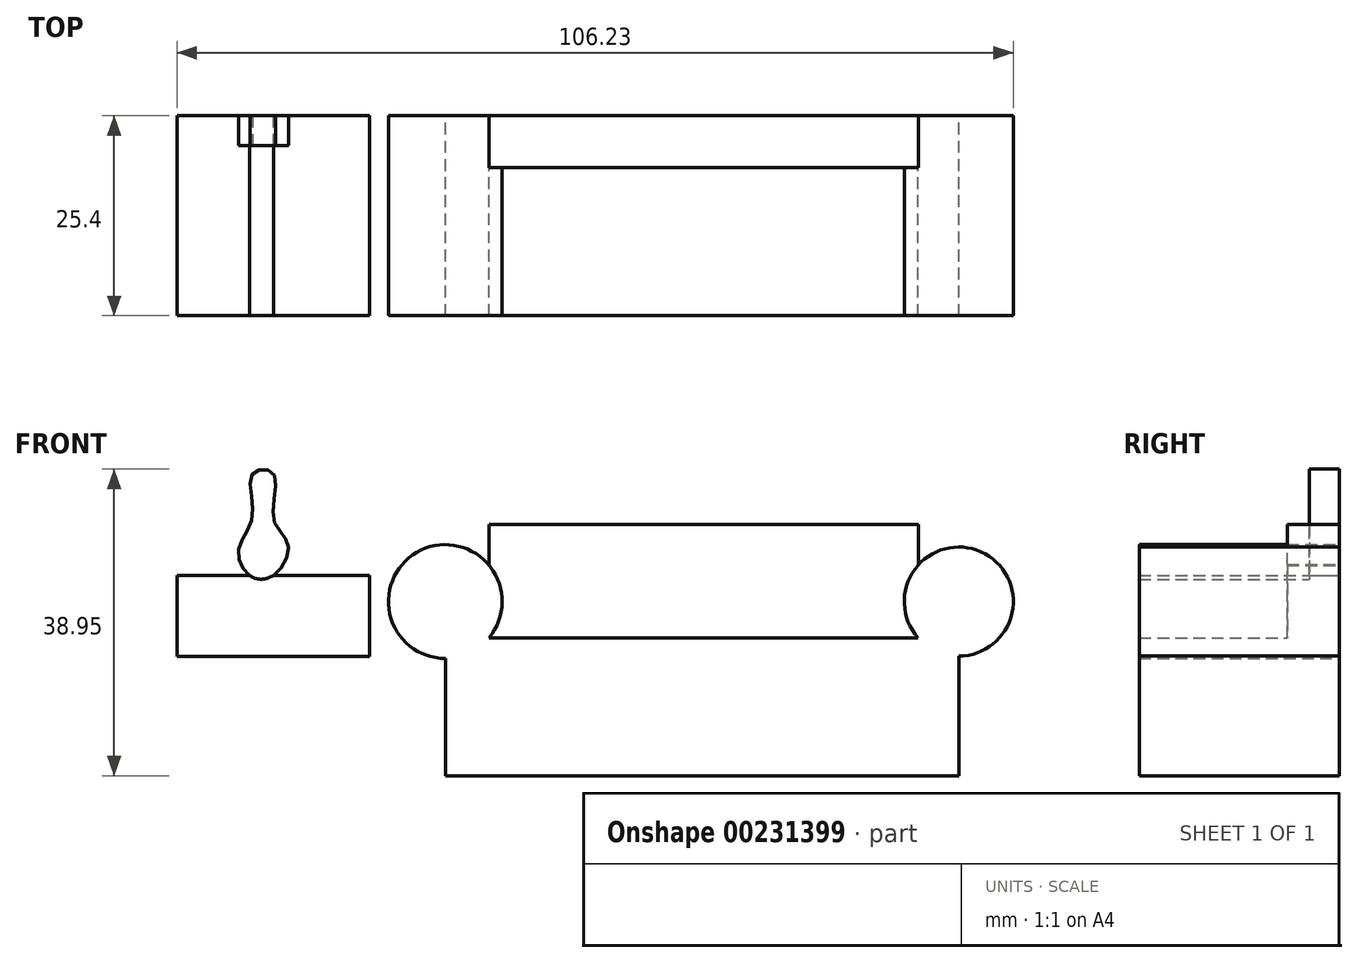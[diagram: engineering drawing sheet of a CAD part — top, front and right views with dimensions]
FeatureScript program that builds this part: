
annotation { "Feature Type Name" : "Feature", "Feature Type Description" : "" }
export const myFeature = defineFeature(function(context is Context, id is Id, definition is map)
    precondition{}
    {
        {
            var Q0;
            Q0=qCreatedBy(makeId("Front.planeOp"),FACE);
            var sketch = newSketch(context, id + "F0", { "sketchPlane" : qUnion([Q0])});
            skLineSegment(sketch, "E0.top", {"start": v(-12.93, -15.18) * mm, "end": v(52.3, -15.18) * mm});
            skLineSegment(sketch, "E0.left", {"start": v(-12.93, -0.27) * mm, "end": v(-12.93, -15.18) * mm});
            skLineSegment(sketch, "E0.right", {"start": v(52.3, 0.03) * mm, "end": v(52.3, -15.18) * mm});
            skCircle(sketch, "E1", {"center": v(-12.93, 6.95) * mm, "radius": 7.22 * mm});
            skCircle(sketch, "E2", {"center": v(52.3, 6.95) * mm, "radius": 6.92 * mm});
            skLineSegment(sketch, "E3", {"start": v(-7.36, 2.35) * mm, "end": v(47.12, 2.35) * mm});
            skLineSegment(sketch, "E4.bottom", {"start": v(-7.36, 2.35) * mm, "end": v(47.2, 2.35) * mm});
            skLineSegment(sketch, "E4.top", {"start": v(-7.36, 16.75) * mm, "end": v(47.2, 16.75) * mm});
            skLineSegment(sketch, "E4.left", {"start": v(-7.36, 11.55) * mm, "end": v(-7.36, 16.75) * mm});
            skLineSegment(sketch, "E4.right", {"start": v(47.2, 11.65) * mm, "end": v(47.2, 16.75) * mm});
            skLineSegment(sketch, "E5.bottom", {"start": v(-47, 10.28) * mm, "end": v(-22.52, 10.28) * mm});
            skLineSegment(sketch, "E5.top", {"start": v(-47, 0) * mm, "end": v(-22.52, 0) * mm});
            skLineSegment(sketch, "E5.left", {"start": v(-47, 10.28) * mm, "end": v(-47, 0) * mm});
            skLineSegment(sketch, "E5.right", {"start": v(-22.52, 10.28) * mm, "end": v(-22.52, 0) * mm});
            skLineSegment(sketch, "E6.bottom", {"start": v(-47, 0) * mm, "end": v(-44.46, 0) * mm});
            skLineSegment(sketch, "E6.top", {"start": v(-47, -15.18) * mm, "end": v(-44.46, -15.18) * mm});
            skLineSegment(sketch, "E6.left", {"start": v(-47, 0) * mm, "end": v(-47, -15.18) * mm});
            skLineSegment(sketch, "E6.right", {"start": v(-44.46, 0) * mm, "end": v(-44.46, -15.18) * mm});
            skLineSegment(sketch, "E7.bottom", {"start": v(-22.52, 0) * mm, "end": v(-25.07, 0) * mm});
            skLineSegment(sketch, "E7.top", {"start": v(-22.52, -15.18) * mm, "end": v(-25.07, -15.18) * mm});
            skLineSegment(sketch, "E7.left", {"start": v(-22.52, 0) * mm, "end": v(-22.52, -15.18) * mm});
            skLineSegment(sketch, "E7.right", {"start": v(-25.07, 0) * mm, "end": v(-25.07, -15.18) * mm});
            skPoint(sketch, "E8.4.internal.snap0", {"position": v(-34.77, 10.28) * mm});
            skPoint(sketch, "E8.5.internal.snap0", {"position": v(-34.77, 10.28) * mm});
            skFitSpline(sketch, "E8", {"points": [v(-37.8, 10.28) * mm, v(-39.17, 13.61) * mm, v(-37.4, 17.92) * mm, v(-37.4, 23.2) * mm, v(-34.77, 23.2) * mm, v(-34.77, 17.53) * mm, v(-32.9, 14.2) * mm, v(-34.77, 10.28) * mm, v(-37.8, 10.28) * mm]});
            skSolve(sketch);
        }
        {
            var Q0;
            Q0=makeQuery(id+"F0.imprint","IMPRINT",FACE,{"disambiguationData":[TD([[makeQuery(id+"F0.imprint","IMPRINT",EDGE,{"derivedFrom":sQuery(id+"F0.wireOp",EDGE,"E5.top")}),1.0]])]});
            var Q1;
            Q1=makeQuery(id+"F0.imprint","IMPRINT",FACE,{"disambiguationData":[TD([[makeQuery(id+"F0.imprint","IMPRINT",EDGE,{"derivedFrom":sQuery(id+"F0.wireOp",EDGE,"E0.top")}),1.0]])]});
            var Q2;
            {var subQ0=sQuery(id+"F0.wireOp",EDGE,"E1");var subQ1=makeQuery(id+"F0.imprint","INTERSECT",VERTEX,{"derivedFrom":[sQuery(id+"F0.wireOp",EDGE,"E0.left"),subQ0]});Q2=makeQuery(id+"F0.imprint","IMPRINT",FACE,{"disambiguationData":[TD([[makeQuery(id+"F0.imprint","IMPRINT",EDGE,{"disambiguationData":[TD([[subQ1,1.0]])],"derivedFrom":subQ0}),1.0]])]});}
            var Q3;
            {var subQ0=sQuery(id+"F0.wireOp",EDGE,"E2");var subQ1=makeQuery(id+"F0.imprint","INTERSECT",VERTEX,{"derivedFrom":[subQ0,sQuery(id+"F0.wireOp",EDGE,"E4.right")]});Q3=makeQuery(id+"F0.imprint","IMPRINT",FACE,{"disambiguationData":[TD([[makeQuery(id+"F0.imprint","IMPRINT",EDGE,{"disambiguationData":[TD([[subQ1,-1.0]])],"derivedFrom":subQ0}),1.0]])]});}
            var Q4;
            Q4=makeQuery(id+"F0.imprint","IMPRINT",FACE,{"disambiguationData":[TD([[makeQuery(id+"F0.imprint","IMPRINT",EDGE,{"derivedFrom":sQuery(id+"F0.wireOp",EDGE,"E7.bottom")}),1.0]])]});
            var Q5;
            Q5=makeQuery(id+"F0.imprint","IMPRINT",FACE,{"disambiguationData":[TD([[makeQuery(id+"F0.imprint","IMPRINT",EDGE,{"derivedFrom":sQuery(id+"F0.wireOp",EDGE,"E6.bottom")}),-1.0]])]});
            extrude(context, id + "F1", {"entities" : qUnion([Q0, Q1, Q2, Q3, Q4, Q5]), "depth" : 25.4 * mm});
        }
        {
            var Q0;
            Q0=makeQuery(id+"F0.imprint","IMPRINT",FACE,{"disambiguationData":[TD([[makeQuery(id+"F0.imprint","IMPRINT",EDGE,{"derivedFrom":sQuery(id+"F0.wireOp",EDGE,"E4.top")}),-1.0]])]});
            extrude(context, id + "F2", {"entities" : qUnion([Q0]), "operationType" : NewBodyOperationType.ADD, "depth" : 6.6 * mm});
        }
        {
            var Q0;
            {var subQ0=sQuery(id+"F0.wireOp",EDGE,"E8");Q0=makeQuery(id+"F0.imprint","IMPRINT",FACE,{"disambiguationData":[TD([[makeQuery(id+"F0.imprint","IMPRINT",EDGE,{"derivedFrom":subQ0}),-1.0]])]});}
            extrude(context, id + "F3", {"entities" : qUnion([Q0]), "operationType" : NewBodyOperationType.ADD, "depth" : 3.8 * mm});
        }
    });
